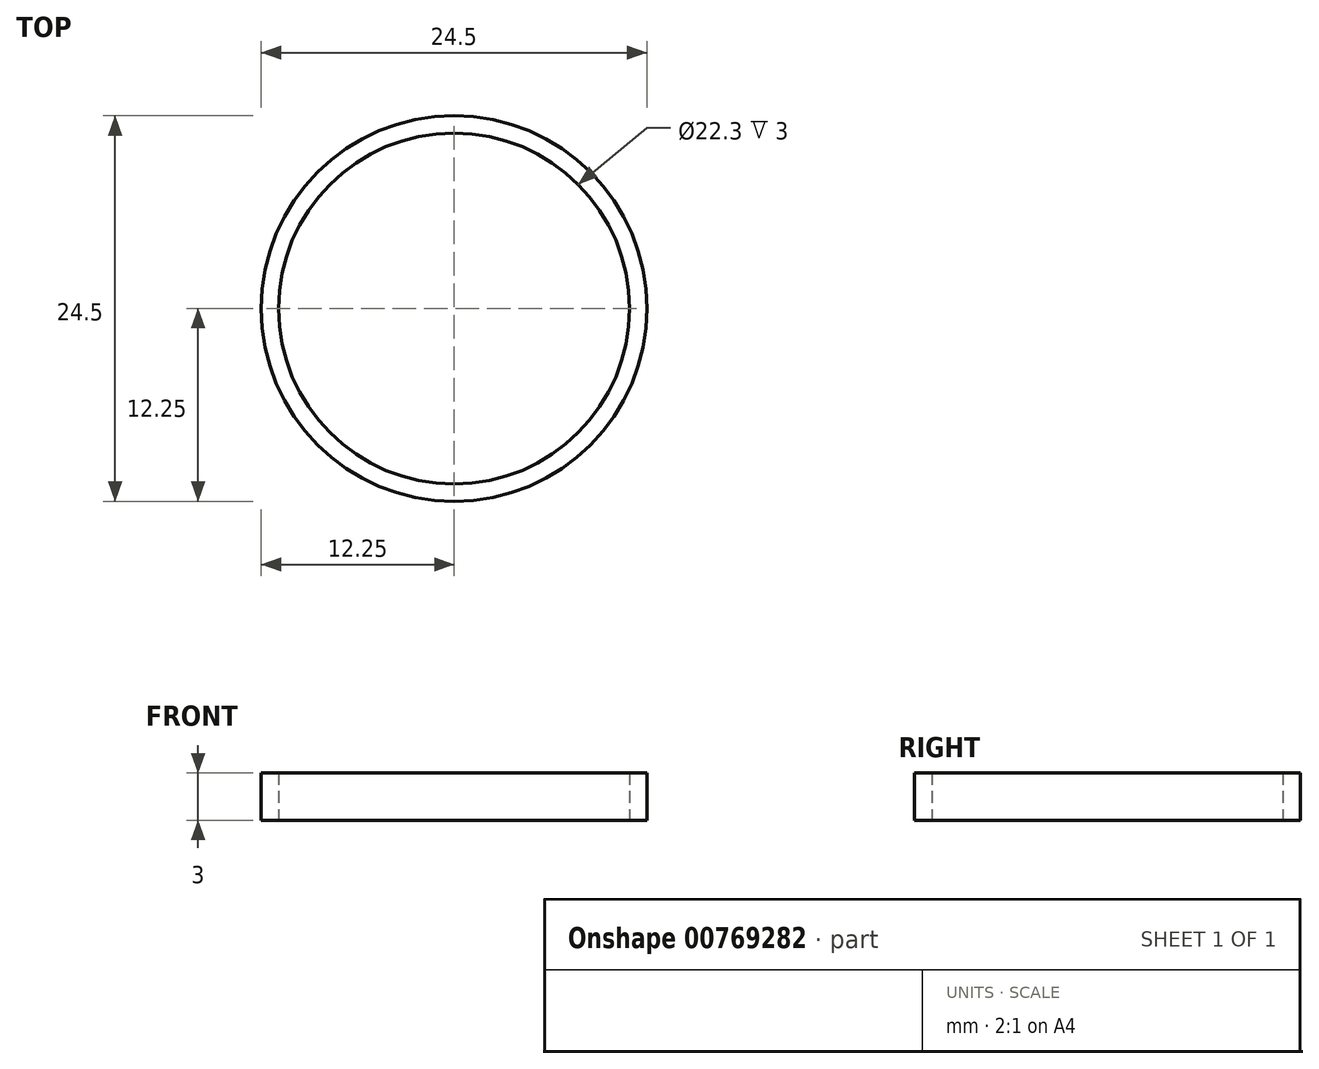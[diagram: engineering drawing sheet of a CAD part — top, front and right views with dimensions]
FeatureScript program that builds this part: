
annotation { "Feature Type Name" : "Feature", "Feature Type Description" : "" }
export const myFeature = defineFeature(function(context is Context, id is Id, definition is map)
    precondition{}
    {
        {
            var Q0;
            Q0=qCreatedBy(makeId("Top.planeOp"),FACE);
            var sketch = newSketch(context, id + "F0", { "sketchPlane" : qUnion([Q0])});
            skCircle(sketch, "E0", {"center": v(0, 0) * mm, "radius": 11.15 * mm});
            skCircle(sketch, "E1", {"center": v(0, 0) * mm, "radius": 12.25 * mm});
            skSolve(sketch);
        }
        {
            var Q0;
            Q0 = qSketchRegion(id + "F0", true);
            extrude(context, id + "F1", {"entities" : qUnion([Q0]), "depth" : 3 * mm, "offsetDistance" : 25 * mm});
        }
    });
